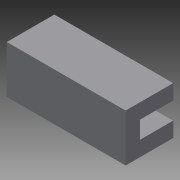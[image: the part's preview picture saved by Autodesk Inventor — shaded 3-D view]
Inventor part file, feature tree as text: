
AUTODESK INVENTOR PART (.ipt)
format: ipt  version: 2015 (Build 190159000, 159)  size: 80,896 bytes
history: native  units: mm
features: extrude x2, sketch x2, other x1
ambient origin geometry x8: Origin, YZ Plane, XZ Plane, XY Plane, X Axis, Y Axis, Z Axis, Center Point
bodies: Body1 (feature_tree)
feature tree (5):
  other  "ソリッド1"
  extrude  "押し出し1"  Depth=75.0mm
  extrude  "押し出し2"  Depth=30.0mm
  sketch  "スケッチ1"
  sketch  "スケッチ2"
